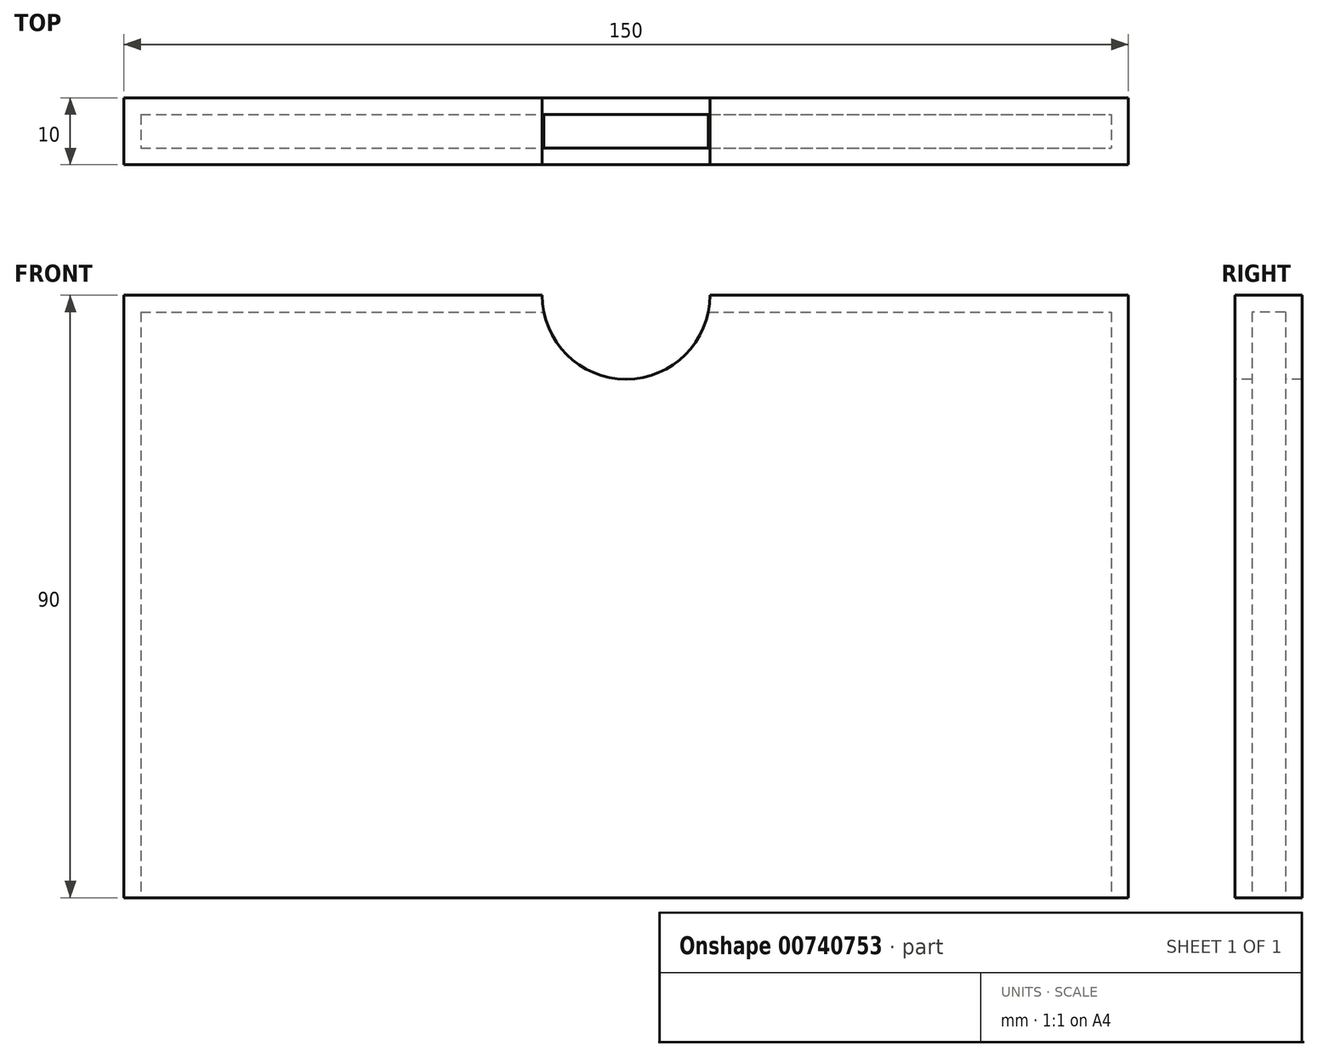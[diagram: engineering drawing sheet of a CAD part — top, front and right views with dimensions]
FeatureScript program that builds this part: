
annotation { "Feature Type Name" : "Feature", "Feature Type Description" : "" }
export const myFeature = defineFeature(function(context is Context, id is Id, definition is map)
    precondition{}
    {
        {
            var Q0;
            Q0=qCreatedBy(makeId("Top.planeOp"),FACE);
            var sketch = newSketch(context, id + "F0", { "sketchPlane" : qUnion([Q0])});
            skLineSegment(sketch, "E0.bottom", {"start": v(-75, 5) * mm, "end": v(75, 5) * mm});
            skLineSegment(sketch, "E0.top", {"start": v(-75, -5) * mm, "end": v(75, -5) * mm});
            skLineSegment(sketch, "E0.left", {"start": v(-75, 5) * mm, "end": v(-75, -5) * mm});
            skLineSegment(sketch, "E0.right", {"start": v(75, 5) * mm, "end": v(75, -5) * mm});
            skPoint(sketch, "E0.middle", {"position": v(0, 0) * mm});
            skSolve(sketch);
        }
        {
            var Q0;
            Q0 = qSketchRegion(id + "F0", true);
            extrude(context, id + "F1", {"entities" : qUnion([Q0]), "depth" : 90 * mm, "offsetDistance" : 25 * mm});
        }
        {
            var Q0;
            Q0=makeQuery(id+"F1.opExtrude","CAP_FACE",FACE,{"disambiguationData":[OSD([sQuery(id+"F0.wireOp",EDGE,"E0.bottom"),sQuery(id+"F0.wireOp",EDGE,"E0.top"),sQuery(id+"F0.wireOp",EDGE,"E0.left"),sQuery(id+"F0.wireOp",EDGE,"E0.right")])],"isStart":true});
            shell(context, id + "F2", {"entities" : qUnion([Q0]), "thickness" : 2.5 * mm});
        }
        {
            var Q0;
            Q0=makeQuery(id+"F1.opExtrude","SWEPT_FACE",FACE,{"disambiguationData":[OSD([sQuery(id+"F0.wireOp",EDGE,"E0.top")])]});
            var sketch = newSketch(context, id + "F3", { "sketchPlane" : qUnion([Q0])});
            skCircle(sketch, "E1", {"center": v(0, 90) * mm, "radius": 12.54 * mm});
            skSolve(sketch);
        }
        {
            var Q0;
            Q0 = qSketchRegion(id + "F3", true);
            extrude(context, id + "F4", {"entities" : qUnion([Q0]), "operationType" : NewBodyOperationType.REMOVE, "oppositeDirection" : true, "depth" : 25 * mm, "offsetDistance" : 25 * mm});
        }
    });
